# Revit family: Verano_V764_Olivera Centre closure_GM_R21
name_source: partatom
category: Generic Models
units: mm (PartAtom-declared; Revit-internal decimal feet)

## family parameters
Always vertical = Yes
Can host rebar = No
Cut with Voids When Loaded = No
Part Type = Normal
Room Calculation Point = No
Round Connector Dimension = Use Diameter
Shared = No
Work Plane-Based = No

## types (1)
- 4 Track
    Default Elevation = 0 mm  [stored 0 ft]
    Description = The Olivera is a sliding glass wall with 8 mm or 10 mm of tempered glass. The glass panels are positioned on a smooth running, anodised rail and are equipped with a transport function. The Olivera can be used with all Verano® patio awnings and various other existing situations.
    Frame Material = V_Antracite
    Manufacturer = Verano Systems
    Maximal Height = 2250 mm
    Maximal Width = 6000 mm  [stored 19.685 ft]
    Minimal Height = 1250 mm  [stored 4.10105 ft]
    Minimal Width = 3000 mm  [stored 9.84252 ft]
    Model = V764 Olivera
    Opening Minimum = 0 mm  [stored 0 ft]
    Opening Percentage % = 50
    Panel Material = Glass
    URL = www.verano.nl

note: [stored X ft] marks values corroborated as IEEE doubles in the binary element streams (Revit-internal decimal feet)

## geometry (parser evidence)
native form markers: Sweep x21
no freeform markers — native parametric forms only
